# Revit family: Door_AcousticWood_Ambico_Single-Vision
name_source: partatom
category: Doors
units: mm (PartAtom-declared; Revit-internal decimal feet)

## family parameters
Always vertical = Yes
Classification Number = 23.30.10.21.17.14
Cut with Voids When Loaded = No
Host = Wall
Room Calculation Point = No
Shared = No

## types (9) — shared parameters
ADA Compliant = Yes
Backset = 0' - 3"
Construction Details = http://www.arcat.com
Exterior Finish = Wood - Red Oak - Ambico - Stained
Frame Finish = Metal - Stainless Steel - Ambico - 4 Finish
Frame Thickness = 0' - 5 7/8"
Frame Width = 0' - 2"
Function = Interior
Glazing Configuration = as Specified
Glazing Tint = Glass - Glazing - Ambico - Clear
Green Building-LEED = http://www.arcat.com
Hardware Finish = Metal - Stainless Steel - Ambico - 4 Finish
Heat Transfer Coefficient (U) = 0.1 BTU/(h·ft²·°F)
Height = 7' - 0"
Installation-Fabrication = http://www.ambico.com
Interior Finish = Wood - Red Oak - Ambico - Stained
Keynote = 08300
Manufacturer = Ambico Limited
Manufacturer Fax = 800-465-8561
Manufacturer Website = http://www.ambico.com
Panel Finish Notes = Exterior is Pull. Interior is Push.
Panel Height = 6' - 11 3/4"
Panel Width = 3' - 0"
Product Data = http://www.arcat.com
R = 0.0000 (h·ft²·°F)/BTU
RO Offset = 0' - 0"
Rough Height = 7' - 0"
Rough Width = 3' - 0"
Sales Information = http://www.ambico.com
Send Message = http://www.arcat.com Limited&coid=40356&rep=119&fax=800-465-8561&mf=
Specification = http://www.arcat.com
Thermal Resistance (R) = 0.0000 (h·ft²·°F)/BTU
U = 0.1 BTU/(h·ft²·°F)
URL = http://www.ambico.com
Vision Lite Height = 2' - 0"
Vision Lite Width = 1' - 0"
Vision Lite from Latch Side = 0' - 6"
Vision Lite from Top = 0' - 6"
Wall Closure = By host
Width = 3' - 0"
zero-valued in all types: Expected Lifespan (Years), Maintenance Schedule (Months), SHGC, Solar Heat Gain Coefficient, VLT, Visual Light Transmittance, Warranty Duration (Years)

## per-type parameters (varying)
| type | Description | Door Rabbet | Fire Rated | Fire Rating | Model | STCValue | Small Trim | Sound Transmission Class (STC) | Thickness |
| STC 33 to 35 | Ambico Acoustic Metal Framed Wood Door - Single as Specified | 0' - 1 15/16" | No | NFR | Acoustic Wood Vision Non Fire Rated | 35 | No | 35 | 0' - 1 3/4" |
| STC 36 to 40 | Ambico Acoustic Metal Framed Wood Door - Single as Specified | 0' - 1 15/16" | No | NFR | Acoustic Wood Vision Non Fire Rated | 40 | No | 40 | 0' - 1 3/4" |
| STC 41 to 46 | Ambico Acoustic Metal Framed Wood Door - Single as Specified | 0' - 1 15/16" | No | NFR | Acoustic Wood Vision Non Fire Rated | 46 | No | 46 | 0' - 1 3/4" |
| STC 47 to 50 | Ambico Acoustic Metal Framed Wood Door - Single as Specified | 0' - 1 15/16" | No | NFR | Acoustic Wood Vision Non Fire Rated | 50 | Yes | 50 | 0' - 1 3/4" |
| STC 51 to 52 | Ambico Acoustic Metal Framed Wood Door - Single as Specified | 0' - 2 7/16" | No | NFR | Acoustic Wood Vision Non Fire Rated | 52 | Yes | 52 | 0' - 2 1/4" |
| STC 53 | Ambico Acoustic Metal Framed Wood Door - Single as Specified | 0' - 2 7/16" | No | NFR | Acoustic Wood Vision Non Fire Rated | 53 | Yes | 53 | 0' - 2 1/4" |
| Fire Rated STC 33 to 35 | Ambico Fire Rated Acoustic Metal Framed Wood Door - Single as Specified | 0' - 1 15/16" | Yes | FR  ;  90 Min | Acoustic Wood Vision Fire Rated | 35 | No | 35 | 0' - 1 3/4" |
| Fire Rated STC 36 to 40 | Ambico Fire Rated Acoustic Metal Framed Wood Door - Single as Specified | 0' - 1 15/16" | Yes | FR  ;  90 Min | Acoustic Wood Vision Fire Rated | 40 | No | 40 | 0' - 1 3/4" |
| Fire Rated STC 41 to 50 | Ambico Fire Rated Acoustic Metal Framed Wood Door - Single as Specified | 0' - 2 7/16" | Yes | FR  ;  90 Min | Acoustic Wood Vision Fire Rated | 50 | Yes | 50 | 0' - 2 1/4" |

## geometry (parser evidence)
native form markers: Blend x14, Sweep x11
no freeform markers — native parametric forms only
